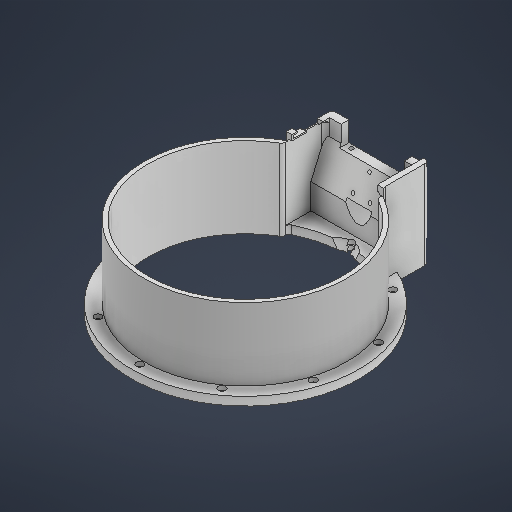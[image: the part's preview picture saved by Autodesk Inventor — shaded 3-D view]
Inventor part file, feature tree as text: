
AUTODESK INVENTOR PART (.ipt)
format: ipt  version: 2025 (Build 290162000, 162)  size: 712,704 bytes
history: native  units: in
note: dims shown in document units (in); Inventor stores cm internally (conversion verified against a paired STEP export)
features: extrude x27, sketch x24, other x3, plane x3, chamfer x3, fillet x1
ambient origin geometry x8: Origin, YZ Plane, XZ Plane, XY Plane, X Axis, Y Axis, Z Axis, Center Point
bodies: Body1 (feature_tree)
feature tree (61):
  other  "Cylinder.ipt"
  extrude  "Extrusion1"  Depth=0.3937in
  extrude  "Extrusion2"  Depth=0.3937in TaperAngle=0.0deg
  sketch  "Sketch3"  dims[d7=11.2205in d8=10.6299in]
  extrude  "Extrusion3"  Depth=10.6299in
  extrude  "Extrusion5"  Depth=0.1969in TaperAngle=0.0deg
  sketch  "Sketch6"  dims[d24=0.1969in d25=0.0in d31=0.0in d32=0.0in]
  extrude  "Extrusion6"  Depth=0.2953in
  extrude  "Extrusion7"  TaperAngle=0.0deg  [1 undecoded]
  extrude  "Extrusion8"  Depth=9.8425in
  plane  "Work Plane1"
  extrude  "Extrusion9"  Depth=10.6299in
  extrude  "Extrusion21"  Depth=0.0787in
  sketch  "Sketch19"  dims[d107=2.2047in d108=0.0in d113=2.5591in]
  extrude  "Extrusion34"  Depth=2.5591in
  extrude  "Extrusion43"  Depth=0.0591in
  extrude  "Extrusion53"  Depth=0.0787in
  extrude  "Extrusion44"  Depth=0.0787in
  extrude  "Extrusion45"  TaperAngle=90.0deg  [1 undecoded]
  chamfer  "Chamfer8"  Distance=1.1614in
  sketch  "Sketch31"  dims[d164=1.5298in d165=0.0787in]
  extrude  "Extrusion46"  Depth=0.0787in
  extrude  "Extrusion47"  Depth=3.937in TaperAngle=360.0deg
  plane  "Work Plane2"
  extrude  "Extrusion48"  Depth=9.065in
  plane  "Work Plane3"
  extrude  "Extrusion51"  Depth=1.8228in
  extrude  "Extrusion54"  Depth=2.564in
  extrude  "Extrusion55"  Depth=3.5433in
  extrude  "Extrusion56"  Depth=3.3661in TaperAngle=0.0deg
  extrude  "Extrusion57"  Depth=3.1496in TaperAngle=0.0deg
  extrude  "Extrusion58"  Depth=0.0787in
  extrude  "Extrusion59"  Depth=0.1575in
  extrude  "Extrusion60"  Depth=0.1575in
  extrude  "Extrusion61"  Depth=0.0787in
  extrude  "Extrusion62"  Depth=0.0787in
  fillet  "Fillet22"  Radius=0.4331in
  chamfer  "Chamfer12"  Distance=0.4331in
  chamfer  "Chamfer13"  Distance=2.1654in
  other  "Solid12::Cylinder.ipt"
  other  "TaggingFeature1"
  sketch  "Sketch1"  dims[d0=0.3937in d2=10.2362in]
  sketch  "Sketch2"  dims[d3=0.0in d4=0.0in d5=0.3937in d6=0.0in]
  sketch  "Sketch5"  dims[d17=10.6299in d18=0.2953in]
  sketch  "Sketch7"  dims[d33=2.1654in d34=0.0in d35=9.8425in]
  sketch  "Sketch9"  dims[d36=10.6299in d46=9.065in]
  sketch  "Sketch14"  dims[d47=0.3937in d48=0.0in d88=0.0787in]
  sketch  "Sketch22"  dims[d117=0.0591in d120=0.5433in]
  sketch  "Sketch Circular Pattern3"  dims[d10=0.1969in d11=0.0in d15=0.1969in d16=0.0in]
  sketch  "Sketch30"  dims[d122=9.4488in d134=0.0787in]
  sketch  "Sketch32"  dims[d166=1.8325in d167=90.0deg d173=1.1614in d174=0.0in]
  sketch  "Sketch35"  dims[d175=0.0787in d209=0.2165in]
  sketch  "Sketch37"  dims[d210=0.3425in d211=3.937in d213=360.0deg]
  sketch  "Sketch38"  dims[d217=10.4151in d218=9.065in]
  sketch  "Sketch39"  dims[d223=0.5433in d224=1.8228in]
  sketch  "Sketch40"  dims[d225=3.5433in d226=2.564in]
  sketch  "Sketch42"  dims[d227=2.7608in d228=3.5433in]
  sketch  "Sketch43"  dims[d233=7.3568in d234=1.5846in d235=0.0in d236=0.0in d237=3.3661in d238=0.3937in d239=0.0in d240=0.0in]
  sketch  "Sketch45"  dims[d241=0.9843in d242=3.1496in d243=0.0in]
  sketch  "Sketch46"  dims[d244=1.5748in d245=0.0787in d246=0.1598in d247=0.4331in]
  sketch  "Sketch47"  dims[d248=0.1575in d249=0.1575in d250=0.1575in d251=0.9331in d255=0.9331in d256=0.4331in d257=0.4331in d258=2.1654in d259=0.0in d260=0.1772in d261=0.0in d263=0.1666in d265=1.5871in d266=0.0in d267=1.5748in d268=0.5315in d269=-3.5433in d277=2.9528in d279=1.5787in d280=0.0in d293=1.378in d306=4.5276in d307=0.0591in d308=2.7608in d309=3.5433in d311=0.3937in d312=0.3937in d313=3.3661in d314=0.3937in d315=0.0in d316=0.0in d317=1.5871in d318=0.0in d319=0.1969in d320=1.1811in d321=0.5906in d322=0.0in d323=0.3937in d324=0.0in d327=0.1772in d328=1.5871in d329=0.0in d330=0.1575in d331=0.0in d332=0.0591in d333=0.1969in d334=0.0in d335=0.1969in d336=0.0in d337=0.0591in d338=0.0591in d339=0.1768in d340=0.0in d341=0.7874in d342=0.0591in d343=0.0591in d344=0.1969in d345=0.0in d346=0.2559in d347=0.0591in d348=0.2559in d349=0.0591in d350=0.1969in d351=0.0in d352=0.1969in d353=0.1575in d354=0.0787in d355=45.0deg d356=0.0787in d357=0.0787in d358=45.0deg d143=0.0197in d144=0.0344in d145=0.0197in d146=0.0344in d153=0.0in d154=0.0in d155=0.0in d156=0.0in d201=0.0197in d202=0.0344in d203=0.0197in d204=0.0344in d215=0.0197in d216=0.0344in d294=0.0197in d295=0.0344in d296=0.0197in d297=0.0344in]
note: 2 required parameter values undecoded (feature->parameter linkage not recoverable at this tier; creation-order binding heuristic only, values carry confidence <= 0.55)
